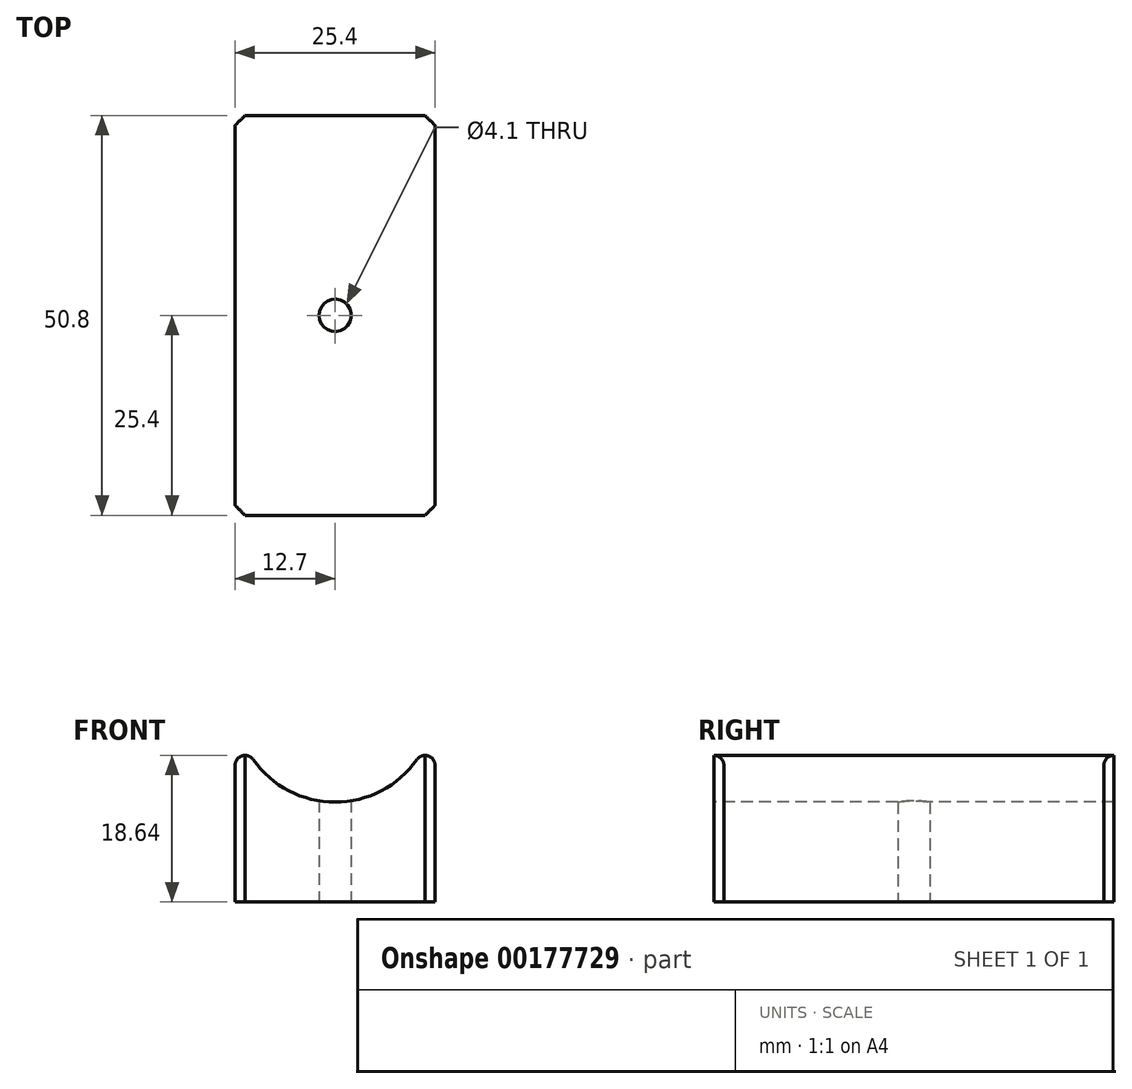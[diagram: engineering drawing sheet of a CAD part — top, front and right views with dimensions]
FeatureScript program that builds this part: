
annotation { "Feature Type Name" : "Feature", "Feature Type Description" : "" }
export const myFeature = defineFeature(function(context is Context, id is Id, definition is map)
    precondition{}
    {
        {
            var Q0;
            Q0=qCreatedBy(makeId("Top.planeOp"),FACE);
            var sketch = newSketch(context, id + "F0", { "sketchPlane" : qUnion([Q0])});
            skLineSegment(sketch, "E0.bottom", {"start": v(0, 0) * mm, "end": v(25.4, 0) * mm});
            skLineSegment(sketch, "E0.top", {"start": v(0, -50.8) * mm, "end": v(25.4, -50.8) * mm});
            skLineSegment(sketch, "E0.left", {"start": v(0, 0) * mm, "end": v(0, -50.8) * mm});
            skLineSegment(sketch, "E0.right", {"start": v(25.4, 0) * mm, "end": v(25.4, -50.8) * mm});
            skSolve(sketch);
        }
        {
            var Q0;
            Q0=makeQuery(id+"F0.imprint","IMPRINT",FACE,{"disambiguationData":[TD([[makeQuery(id+"F0.imprint","IMPRINT",EDGE,{"derivedFrom":sQuery(id+"F0.wireOp",EDGE,"E0.bottom")}),-1.0]])]});
            extrude(context, id + "F1", {"entities" : qUnion([Q0]), "depth" : 25.4 * mm});
        }
        {
            var Q0;
            Q0=makeQuery(id+"F1.opExtrude","SWEPT_FACE",FACE,{"disambiguationData":[OSD([sQuery(id+"F0.wireOp",EDGE,"E0.top")])]});
            var sketch = newSketch(context, id + "F2", { "sketchPlane" : qUnion([Q0])});
            skCircle(sketch, "E1", {"center": v(12.7, 25.4) * mm, "radius": 12.7 * mm});
            skSolve(sketch);
        }
        {
            var Q0;
            {var subQ1=sQuery(id+"F0.wireOp",EDGE,"E0.top");var subQ2=makeQuery(id+"F1.opExtrude","CAP_EDGE",EDGE,{"disambiguationData":[OSD([subQ1])],"isStart":false});Q0=makeQuery(id+"F2.imprint","IMPRINT",FACE,{"disambiguationData":[TD([[makeQuery(id+"F2.imprint","IMPRINT",EDGE,{"derivedFrom":subQ2}),-1.0]])]});}
            extrude(context, id + "F3", {"entities" : qUnion([Q0]), "operationType" : NewBodyOperationType.REMOVE, "oppositeDirection" : true, "depth" : 50.8 * mm});
        }
        {
            var Q0;
            Q0=makeQuery(id+"F1.opExtrude","CAP_FACE",FACE,{"disambiguationData":[OSD([sQuery(id+"F0.wireOp",EDGE,"E0.bottom"),sQuery(id+"F0.wireOp",EDGE,"E0.top"),sQuery(id+"F0.wireOp",EDGE,"E0.left"),sQuery(id+"F0.wireOp",EDGE,"E0.right")])],"isStart":true});
            var sketch = newSketch(context, id + "F4", { "sketchPlane" : qUnion([Q0])});
            skPoint(sketch, "E2", {"position": v(12.7, 25.4) * mm});
            skPoint(sketch, "E2.positionSnap0", {"position": v(12.7, 0) * mm});
            skPoint(sketch, "E2.positionSnap1", {"position": v(0, 25.4) * mm});
            skSolve(sketch);
        }
        {
            var Q0;
            Q0=sQuery(id+"F4.wireOp",VERTEX,"E2");
            var Q1;
            Q1=makeQuery(id+"F1.opExtrude","SWEPT_BODY",BODY,{"disambiguationData":[OSD([sQuery(id+"F0.wireOp",EDGE,"E0.bottom"),sQuery(id+"F0.wireOp",EDGE,"E0.top"),sQuery(id+"F0.wireOp",EDGE,"E0.left"),sQuery(id+"F0.wireOp",EDGE,"E0.right")])]});
            hole(context, id + "F5", {"style" : HoleStyle.SIMPLE, "endStyle" : HoleEndStyle.THROUGH, "standardTappedOrClearance" : lookupTablePath({ "standard" : "ISO", "engagement" : "75%", "pitch" : "0.9 mm", "size" : "M5", "type" : "Tapped" }), "standardBlindInLast" : lookupTablePath({ "standard" : "ISO", "engagement" : "75%", "pitch" : "0.9 mm", "size" : "M5", "type" : "Tapped" }), "holeDiameter" : 4.1 * mm, "locations" : qUnion([Q0]), "scope" : qUnion([Q1]), "isTappedThrough" : true, "showTappedDepth" : true});
        }
        {
            var Q0;
            {var subQ0=sQuery(id+"F0.wireOp",EDGE,"E0.left");Q0=makeQuery(id+"F3.boolean.opBoolean","MERGE",EDGE,{"derivedFrom":[makeQuery(id+"F1.opExtrude","CAP_EDGE",EDGE,{"disambiguationData":[OSD([subQ0])],"isStart":false}),makeQuery(id+"F3.opExtrude","SWEPT_EDGE",EDGE,{"disambiguationData":[OSD([sQuery(id+"F0.wireOp",EDGE,"E0.top"),subQ0,sQuery(id+"F2.wireOp",EDGE,"E1")])]})]});}
            var Q1;
            {var subQ0=sQuery(id+"F0.wireOp",EDGE,"E0.right");Q1=makeQuery(id+"F3.boolean.opBoolean","MERGE",EDGE,{"derivedFrom":[makeQuery(id+"F1.opExtrude","CAP_EDGE",EDGE,{"disambiguationData":[OSD([subQ0])],"isStart":false}),makeQuery(id+"F3.opExtrude","SWEPT_EDGE",EDGE,{"disambiguationData":[OSD([sQuery(id+"F0.wireOp",EDGE,"E0.top"),subQ0,sQuery(id+"F2.wireOp",EDGE,"E1")])]})]});}
            fillet(context, id + "F6", {"entities" : qUnion([Q0, Q1]), "radius" : 1.27 * mm, "tangentPropagation" : true, "allowEdgeOverflow" : false});
        }
        {
            var Q0;
            Q0=makeQuery(id+"F1.opExtrude","SWEPT_EDGE",EDGE,{"disambiguationData":[OSD([sQuery(id+"F0.wireOp",EDGE,"E0.top"),sQuery(id+"F0.wireOp",EDGE,"E0.right")])]});
            var Q1;
            Q1=makeQuery(id+"F1.opExtrude","SWEPT_EDGE",EDGE,{"disambiguationData":[OSD([sQuery(id+"F0.wireOp",EDGE,"E0.top"),sQuery(id+"F0.wireOp",EDGE,"E0.left")])]});
            var Q2;
            Q2=makeQuery(id+"F1.opExtrude","SWEPT_EDGE",EDGE,{"disambiguationData":[OSD([sQuery(id+"F0.wireOp",EDGE,"E0.bottom"),sQuery(id+"F0.wireOp",EDGE,"E0.right")])]});
            var Q3;
            Q3=makeQuery(id+"F1.opExtrude","SWEPT_EDGE",EDGE,{"disambiguationData":[OSD([sQuery(id+"F0.wireOp",EDGE,"E0.bottom"),sQuery(id+"F0.wireOp",EDGE,"E0.left")])]});
            chamfer(context, id + "F7", {"entities" : qUnion([Q0, Q1, Q2, Q3]), "width" : 1.27 * mm});
        }
    });
